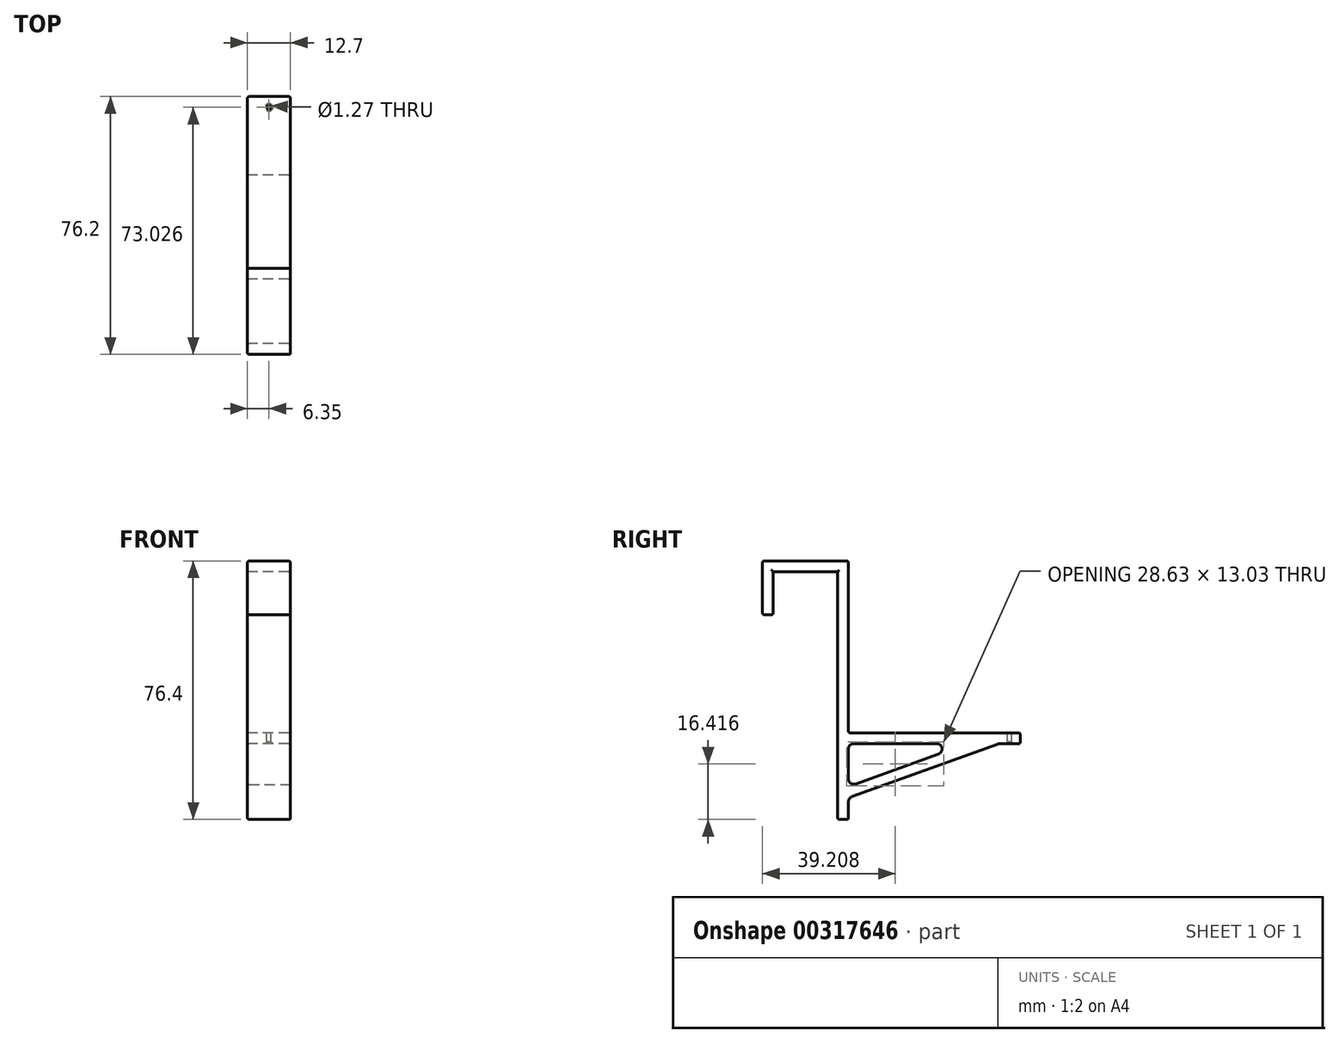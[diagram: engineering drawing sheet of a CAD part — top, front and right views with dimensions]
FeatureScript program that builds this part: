
annotation { "Feature Type Name" : "Feature", "Feature Type Description" : "" }
export const myFeature = defineFeature(function(context is Context, id is Id, definition is map)
    precondition{}
    {
        {
            var Q0;
            Q0=qCreatedBy(makeId("Right.planeOp"),FACE);
            var sketch = newSketch(context, id + "F0", { "sketchPlane" : qUnion([Q0])});
            skLineSegment(sketch, "E0.bottom", {"start": v(-29.59, 49.63) * mm, "end": v(-26.41, 49.63) * mm});
            skLineSegment(sketch, "E0.top", {"start": v(-29.59, 33.75) * mm, "end": v(-26.41, 33.75) * mm});
            skLineSegment(sketch, "E0.left", {"start": v(-29.59, 49.63) * mm, "end": v(-29.59, 33.75) * mm});
            skLineSegment(sketch, "E0.right", {"start": v(-26.41, 49.63) * mm, "end": v(-26.41, 33.75) * mm});
            skLineSegment(sketch, "E1.bottom", {"start": v(-26.41, 49.63) * mm, "end": v(-7.36, 49.63) * mm});
            skLineSegment(sketch, "E1.top", {"start": v(-26.41, 46.45) * mm, "end": v(-7.36, 46.45) * mm});
            skLineSegment(sketch, "E1.left", {"start": v(-26.41, 49.63) * mm, "end": v(-26.41, 46.45) * mm});
            skLineSegment(sketch, "E1.right", {"start": v(-7.36, 49.63) * mm, "end": v(-7.36, 46.45) * mm});
            skLineSegment(sketch, "E2.bottom", {"start": v(-7.36, 49.63) * mm, "end": v(-4.19, 49.63) * mm});
            skLineSegment(sketch, "E2.top", {"start": v(-7.36, -26.77) * mm, "end": v(-4.19, -26.77) * mm});
            skLineSegment(sketch, "E2.left", {"start": v(-7.36, 49.63) * mm, "end": v(-7.36, -26.77) * mm});
            skLineSegment(sketch, "E2.right", {"start": v(-4.19, 49.63) * mm, "end": v(-4.19, -26.77) * mm});
            skLineSegment(sketch, "E3.bottom", {"start": v(-4.19, -1.17) * mm, "end": v(46.61, -1.17) * mm});
            skLineSegment(sketch, "E3.top", {"start": v(-4.19, -4.35) * mm, "end": v(46.61, -4.35) * mm});
            skLineSegment(sketch, "E3.left", {"start": v(-4.19, -1.17) * mm, "end": v(-4.19, -4.35) * mm});
            skLineSegment(sketch, "E3.right", {"start": v(46.61, -1.17) * mm, "end": v(46.61, -4.35) * mm});
            skLineSegment(sketch, "E4", {"start": v(-4.19, -20.42) * mm, "end": v(40.26, -4.35) * mm});
            skLineSegment(sketch, "E5.0", {"start": v(-4.19, -17.05) * mm, "end": v(30.93, -4.35) * mm});
            skSolve(sketch);
        }
        {
            var Q0;
            Q0=makeQuery(id+"F0.imprint","IMPRINT",FACE,{"disambiguationData":[TD([[makeQuery(id+"F0.imprint","IMPRINT",EDGE,{"derivedFrom":sQuery(id+"F0.wireOp",EDGE,"E0.bottom")}),-1.0]])]});
            var Q1;
            {var subQ0=sQuery(id+"F0.wireOp",EDGE,"E1.bottom");Q1=makeQuery(id+"F0.imprint","IMPRINT",FACE,{"disambiguationData":[TD([[makeQuery(id+"F0.imprint","IMPRINT",EDGE,{"derivedFrom":subQ0}),-1.0]])]});}
            var Q2;
            {var subQ3=sQuery(id+"F0.wireOp",EDGE,"E2.bottom");Q2=makeQuery(id+"F0.imprint","IMPRINT",FACE,{"disambiguationData":[TD([[makeQuery(id+"F0.imprint","IMPRINT",EDGE,{"derivedFrom":subQ3}),-1.0]])]});}
            var Q3;
            Q3=makeQuery(id+"F0.imprint","IMPRINT",FACE,{"disambiguationData":[TD([[makeQuery(id+"F0.imprint","IMPRINT",EDGE,{"derivedFrom":sQuery(id+"F0.wireOp",EDGE,"E3.bottom")}),-1.0]])]});
            var Q4;
            {var subQ0=sQuery(id+"F0.wireOp",EDGE,"E4");Q4=makeQuery(id+"F0.imprint","IMPRINT",FACE,{"disambiguationData":[TD([[makeQuery(id+"F0.imprint","IMPRINT",EDGE,{"derivedFrom":subQ0}),1.0]])]});}
            extrude(context, id + "F1", {"entities" : qUnion([Q0, Q1, Q2, Q3, Q4]), "depth" : 12.7 * mm});
        }
        {
            var Q0;
            Q0=makeQuery(id+"F1.opExtrude","SWEPT_EDGE",EDGE,{"disambiguationData":[OSD([sQuery(id+"F0.wireOp",EDGE,"E2.right"),sQuery(id+"F0.wireOp",EDGE,"E3.top"),sQuery(id+"F0.wireOp",EDGE,"E3.left")])]});
            var Q1;
            Q1=makeQuery(id+"F1.opExtrude","SWEPT_EDGE",EDGE,{"disambiguationData":[OSD([sQuery(id+"F0.wireOp",EDGE,"E3.top"),sQuery(id+"F0.wireOp",EDGE,"E5.0")])]});
            var Q2;
            Q2=makeQuery(id+"F1.opExtrude","SWEPT_EDGE",EDGE,{"disambiguationData":[OSD([sQuery(id+"F0.wireOp",EDGE,"E2.right"),sQuery(id+"F0.wireOp",EDGE,"E5.0")])]});
            var Q3;
            Q3=makeQuery(id+"F1.opExtrude","SWEPT_EDGE",EDGE,{"disambiguationData":[OSD([sQuery(id+"F0.wireOp",EDGE,"E2.right"),sQuery(id+"F0.wireOp",EDGE,"E4")])]});
            var Q4;
            Q4=makeQuery(id+"F1.opExtrude","SWEPT_EDGE",EDGE,{"disambiguationData":[OSD([sQuery(id+"F0.wireOp",EDGE,"E3.top"),sQuery(id+"F0.wireOp",EDGE,"E4")])]});
            fillet(context, id + "F2", {"entities" : qUnion([Q0, Q1, Q2, Q3, Q4]), "radius" : 1.59 * mm, "tangentPropagation" : true, "allowEdgeOverflow" : false});
        }
        {
            var Q0;
            Q0=makeQuery(id+"F1.opExtrude","SWEPT_FACE",FACE,{"disambiguationData":[OSD([sQuery(id+"F0.wireOp",EDGE,"E3.bottom")])]});
            var sketch = newSketch(context, id + "F3", { "sketchPlane" : qUnion([Q0])});
            skCircle(sketch, "E6", {"center": v(6.35, 43.44) * mm, "radius": 0.64 * mm});
            skPoint(sketch, "E6.centerSnap0", {"position": v(6.35, 46.61) * mm});
            skSolve(sketch);
        }
        {
            var Q0;
            Q0=makeQuery(id+"F3.imprint","IMPRINT",FACE,{"disambiguationData":[TD([[makeQuery(id+"F3.imprint","IMPRINT",EDGE,{"derivedFrom":sQuery(id+"F3.wireOp",EDGE,"E6")}),1.0]])]});
            extrude(context, id + "F4", {"entities" : qUnion([Q0]), "operationType" : NewBodyOperationType.REMOVE, "oppositeDirection" : true, "depth" : 25.4 * mm});
        }
        {
            var Q0;
            {var subQ0=sQuery(id+"F0.wireOp",EDGE,"E3.top");Q0=makeQuery(id+"F4.boolean.opBoolean","INTERSECT",EDGE,{"derivedFrom":[makeQuery(id+"F1.opExtrude","SWEPT_FACE",FACE,{"disambiguationData":[OSD([subQ0]),TDD([makeQuery(id+"F0.imprint","IMPRINT",EDGE,{"disambiguationData":[TD([[makeQuery(id+"F0.imprint","INTERSECT",VERTEX,{"derivedFrom":[subQ0,sQuery(id+"F0.wireOp",EDGE,"E3.right")]}),1.0]])],"derivedFrom":subQ0})])]}),makeQuery(id+"F4.opExtrude","SWEPT_FACE",FACE,{"disambiguationData":[OSD([sQuery(id+"F3.wireOp",EDGE,"E6")])]})]});}
            chamfer(context, id + "F5", {"entities" : qUnion([Q0]), "width" : 0.5 * mm, "tangentPropagation" : true});
        }
        {
            var Q0;
            Q0=makeQuery(id+"F1.opExtrude","CAP_EDGE",EDGE,{"disambiguationData":[OSD([sQuery(id+"F0.wireOp",EDGE,"E0.left")])],"isStart":false});
            var Q1;
            Q1=makeQuery(id+"F1.opExtrude","CAP_EDGE",EDGE,{"disambiguationData":[OSD([sQuery(id+"F0.wireOp",EDGE,"E0.bottom"),sQuery(id+"F0.wireOp",EDGE,"E1.bottom"),sQuery(id+"F0.wireOp",EDGE,"E2.bottom")])],"isStart":false});
            var Q2;
            {var subQ0=sQuery(id+"F0.wireOp",EDGE,"E2.right");Q2=makeQuery(id+"F1.opExtrude","CAP_EDGE",EDGE,{"disambiguationData":[OSD([subQ0]),TDD([makeQuery(id+"F0.imprint","IMPRINT",EDGE,{"disambiguationData":[TD([[makeQuery(id+"F0.imprint","INTERSECT",VERTEX,{"derivedFrom":[sQuery(id+"F0.wireOp",EDGE,"E2.bottom"),subQ0]}),-1.0]])],"derivedFrom":subQ0})])],"isStart":false});}
            var Q3;
            Q3=makeQuery(id+"F1.opExtrude","CAP_EDGE",EDGE,{"disambiguationData":[OSD([sQuery(id+"F0.wireOp",EDGE,"E3.bottom")])],"isStart":false});
            var Q4;
            Q4=makeQuery(id+"F1.opExtrude","CAP_EDGE",EDGE,{"disambiguationData":[OSD([sQuery(id+"F0.wireOp",EDGE,"E3.right")])],"isStart":false});
            var Q5;
            Q5=makeQuery(id+"F1.opExtrude","CAP_FACE",FACE,{"disambiguationData":[OSD([sQuery(id+"F0.wireOp",EDGE,"E0.bottom"),sQuery(id+"F0.wireOp",EDGE,"E0.top"),sQuery(id+"F0.wireOp",EDGE,"E0.left"),sQuery(id+"F0.wireOp",EDGE,"E0.right"),sQuery(id+"F0.wireOp",EDGE,"E1.bottom"),sQuery(id+"F0.wireOp",EDGE,"E1.top"),sQuery(id+"F0.wireOp",EDGE,"E2.bottom"),sQuery(id+"F0.wireOp",EDGE,"E2.top"),sQuery(id+"F0.wireOp",EDGE,"E2.left"),sQuery(id+"F0.wireOp",EDGE,"E2.right"),sQuery(id+"F0.wireOp",EDGE,"E3.bottom"),sQuery(id+"F0.wireOp",EDGE,"E3.top"),sQuery(id+"F0.wireOp",EDGE,"E3.right"),sQuery(id+"F0.wireOp",EDGE,"E4"),sQuery(id+"F0.wireOp",EDGE,"E5.0")])],"isStart":false});
            var Q6;
            Q6=makeQuery(id+"F1.opExtrude","CAP_FACE",FACE,{"disambiguationData":[OSD([sQuery(id+"F0.wireOp",EDGE,"E0.bottom"),sQuery(id+"F0.wireOp",EDGE,"E0.top"),sQuery(id+"F0.wireOp",EDGE,"E0.left"),sQuery(id+"F0.wireOp",EDGE,"E0.right"),sQuery(id+"F0.wireOp",EDGE,"E1.bottom"),sQuery(id+"F0.wireOp",EDGE,"E1.top"),sQuery(id+"F0.wireOp",EDGE,"E2.bottom"),sQuery(id+"F0.wireOp",EDGE,"E2.top"),sQuery(id+"F0.wireOp",EDGE,"E2.left"),sQuery(id+"F0.wireOp",EDGE,"E2.right"),sQuery(id+"F0.wireOp",EDGE,"E3.bottom"),sQuery(id+"F0.wireOp",EDGE,"E3.top"),sQuery(id+"F0.wireOp",EDGE,"E3.right"),sQuery(id+"F0.wireOp",EDGE,"E4"),sQuery(id+"F0.wireOp",EDGE,"E5.0")])],"isStart":true});
            var Q7;
            Q7=makeQuery(id+"F1.opExtrude","SWEPT_EDGE",EDGE,{"disambiguationData":[OSD([sQuery(id+"F0.wireOp",EDGE,"E0.bottom"),sQuery(id+"F0.wireOp",EDGE,"E0.left")])]});
            var Q8;
            Q8=makeQuery(id+"F1.opExtrude","SWEPT_EDGE",EDGE,{"disambiguationData":[OSD([sQuery(id+"F0.wireOp",EDGE,"E0.top"),sQuery(id+"F0.wireOp",EDGE,"E0.left")])]});
            var Q9;
            Q9=makeQuery(id+"F1.opExtrude","SWEPT_EDGE",EDGE,{"disambiguationData":[OSD([sQuery(id+"F0.wireOp",EDGE,"E2.bottom"),sQuery(id+"F0.wireOp",EDGE,"E2.right")])]});
            var Q10;
            Q10=makeQuery(id+"F1.opExtrude","SWEPT_EDGE",EDGE,{"disambiguationData":[OSD([sQuery(id+"F0.wireOp",EDGE,"E3.bottom"),sQuery(id+"F0.wireOp",EDGE,"E3.right")])]});
            var Q11;
            Q11=makeQuery(id+"F1.opExtrude","SWEPT_EDGE",EDGE,{"disambiguationData":[OSD([sQuery(id+"F0.wireOp",EDGE,"E3.top"),sQuery(id+"F0.wireOp",EDGE,"E3.right")])]});
            var Q12;
            Q12=makeQuery(id+"F1.opExtrude","SWEPT_EDGE",EDGE,{"disambiguationData":[OSD([sQuery(id+"F0.wireOp",EDGE,"E2.right"),sQuery(id+"F0.wireOp",EDGE,"E3.bottom"),sQuery(id+"F0.wireOp",EDGE,"E3.left")])]});
            var Q13;
            Q13=makeQuery(id+"F1.opExtrude","SWEPT_FACE",FACE,{"disambiguationData":[OSD([sQuery(id+"F0.wireOp",EDGE,"E2.top")])]});
            var Q14;
            Q14=makeQuery(id+"F1.opExtrude","SWEPT_EDGE",EDGE,{"disambiguationData":[OSD([sQuery(id+"F0.wireOp",EDGE,"E0.top"),sQuery(id+"F0.wireOp",EDGE,"E0.right")])]});
            fillet(context, id + "F6", {"entities" : qUnion([Q0, Q1, Q2, Q3, Q4, Q5, Q6, Q7, Q8, Q9, Q10, Q11, Q12, Q13, Q14]), "radius" : 0.5 * mm, "tangentPropagation" : true, "allowEdgeOverflow" : false});
        }
    });
